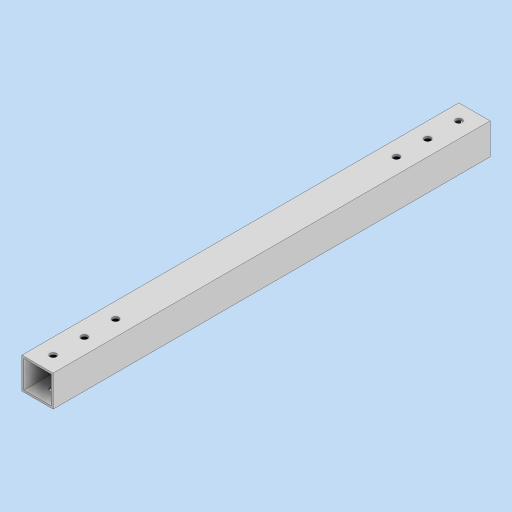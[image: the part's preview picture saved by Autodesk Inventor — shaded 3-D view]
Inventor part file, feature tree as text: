
AUTODESK INVENTOR PART (.ipt)
format: ipt  version: 2024 (Build 280153000, 153)  size: 119,296 bytes
history: native  units: in
note: dims shown in document units (in); Inventor stores cm internally (conversion verified against a paired STEP export)
features: extrude x2, sketch x2, projected_geometry x1
ambient origin geometry x8: Origin, YZ Plane, XZ Plane, XY Plane, X Axis, Y Axis, Z Axis, Center Point
bodies: Solid1 (feature_tree)
feature tree (5):
  extrude  "Extrusion1"  Depth=1.0in
  extrude  "Extrusion2"  Depth=14.0in TaperAngle=0.0deg
  sketch  "Sketch1"  dims[d0=1.0in d1=1.0in]
  sketch  "Sketch2"  dims[d2=0.0625in d3=14.0in d4=0.0in d5=0.203in d6=0.203in d7=0.5in d8=1.0in d9=1.0in d10=0.5in d11=0.0in d12=0.0in]
  projected_geometry  "Projected Loop1"
